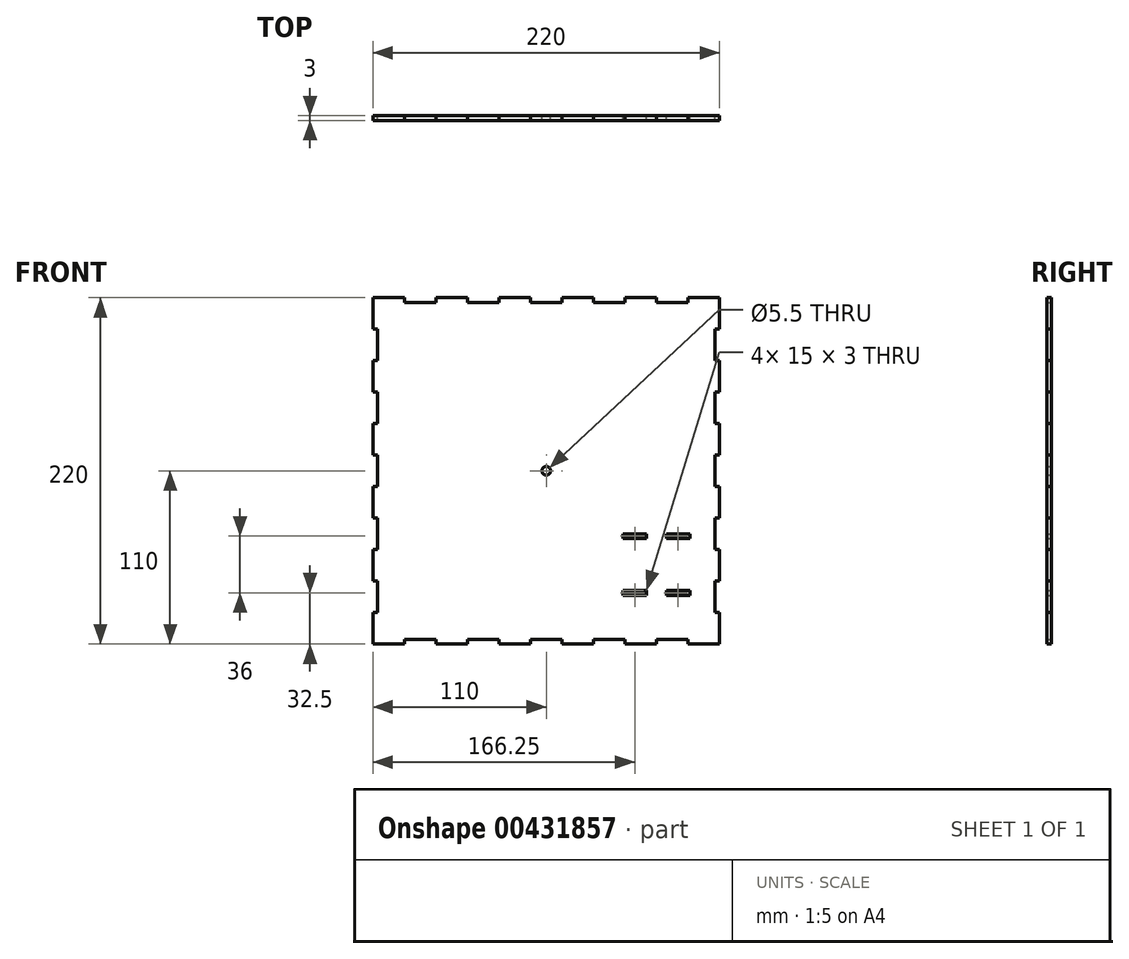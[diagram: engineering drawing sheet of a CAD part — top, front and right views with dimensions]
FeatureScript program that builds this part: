
annotation { "Feature Type Name" : "Feature", "Feature Type Description" : "" }
export const myFeature = defineFeature(function(context is Context, id is Id, definition is map)
    precondition{}
    {
        {
            var Q0;
            Q0=qCreatedBy(makeId("Front.planeOp"),FACE);
            var sketch = newSketch(context, id + "F0", { "sketchPlane" : qUnion([Q0])});
            skLineSegment(sketch, "E0.bottom", {"start": v(-110, 110) * mm, "end": v(-90, 110) * mm});
            skLineSegment(sketch, "E0.top", {"start": v(-110, -110) * mm, "end": v(-90, -110) * mm});
            skLineSegment(sketch, "E0.left", {"start": v(-110, 110) * mm, "end": v(-110, 90) * mm});
            skLineSegment(sketch, "E0.right", {"start": v(110, 110) * mm, "end": v(110, 90) * mm});
            skPoint(sketch, "E0.middle", {"position": v(0, 0) * mm});
            skCircle(sketch, "E1", {"center": v(0, 0) * mm, "radius": 2.75 * mm});
            skLineSegment(sketch, "E2.bottom", {"start": v(63.75, -40) * mm, "end": v(48.75, -40) * mm});
            skLineSegment(sketch, "E2.top", {"start": v(63.75, -43) * mm, "end": v(48.75, -43) * mm});
            skLineSegment(sketch, "E2.left", {"start": v(63.75, -40) * mm, "end": v(63.75, -43) * mm});
            skLineSegment(sketch, "E2.right", {"start": v(48.75, -40) * mm, "end": v(48.75, -43) * mm});
            skLineSegment(sketch, "E3.bottom", {"start": v(76.25, -40) * mm, "end": v(91.25, -40) * mm});
            skLineSegment(sketch, "E3.top", {"start": v(76.25, -43) * mm, "end": v(91.25, -43) * mm});
            skLineSegment(sketch, "E3.left", {"start": v(76.25, -40) * mm, "end": v(76.25, -43) * mm});
            skLineSegment(sketch, "E3.right", {"start": v(91.25, -40) * mm, "end": v(91.25, -43) * mm});
            skLineSegment(sketch, "E4.bottom", {"start": v(48.75, -76) * mm, "end": v(63.75, -76) * mm});
            skLineSegment(sketch, "E4.top", {"start": v(48.75, -79) * mm, "end": v(63.75, -79) * mm});
            skLineSegment(sketch, "E4.left", {"start": v(48.75, -76) * mm, "end": v(48.75, -79) * mm});
            skLineSegment(sketch, "E4.right", {"start": v(63.75, -76) * mm, "end": v(63.75, -79) * mm});
            skLineSegment(sketch, "E5.bottom", {"start": v(91.25, -76) * mm, "end": v(76.25, -76) * mm});
            skLineSegment(sketch, "E5.top", {"start": v(91.25, -79) * mm, "end": v(76.25, -79) * mm});
            skLineSegment(sketch, "E5.left", {"start": v(91.25, -76) * mm, "end": v(91.25, -79) * mm});
            skLineSegment(sketch, "E5.right", {"start": v(76.25, -76) * mm, "end": v(76.25, -79) * mm});
            skLineSegment(sketch, "E6.bottom", {"start": v(-10, -107) * mm, "end": v(10, -107) * mm});
            skLineSegment(sketch, "E6.left", {"start": v(-10, -107) * mm, "end": v(-10, -110) * mm});
            skLineSegment(sketch, "E6.right", {"start": v(10, -107) * mm, "end": v(10, -110) * mm});
            skPoint(sketch, "E6.middle", {"position": v(0, -110) * mm});
            skLineSegment(sketch, "E7.bottom", {"start": v(-50, -107) * mm, "end": v(-30, -107) * mm});
            skLineSegment(sketch, "E7.left", {"start": v(-50, -107) * mm, "end": v(-50, -110) * mm});
            skLineSegment(sketch, "E7.right", {"start": v(-30, -107) * mm, "end": v(-30, -110) * mm});
            skPoint(sketch, "E7.middle", {"position": v(-40, -110) * mm});
            skLineSegment(sketch, "E8.bottom", {"start": v(-90, -107) * mm, "end": v(-70, -107) * mm});
            skLineSegment(sketch, "E8.left", {"start": v(-90, -107) * mm, "end": v(-90, -110) * mm});
            skLineSegment(sketch, "E8.right", {"start": v(-70, -107) * mm, "end": v(-70, -110) * mm});
            skPoint(sketch, "E8.middle", {"position": v(-80, -110) * mm});
            skLineSegment(sketch, "E9.bottom", {"start": v(50, -107) * mm, "end": v(30, -107) * mm});
            skLineSegment(sketch, "E9.left", {"start": v(50, -107) * mm, "end": v(50, -110) * mm});
            skLineSegment(sketch, "E9.right", {"start": v(30, -107) * mm, "end": v(30, -110) * mm});
            skPoint(sketch, "E9.middle", {"position": v(40, -110) * mm});
            skLineSegment(sketch, "E10.bottom", {"start": v(70, -107) * mm, "end": v(90, -107) * mm});
            skLineSegment(sketch, "E10.left", {"start": v(70, -107) * mm, "end": v(70, -110) * mm});
            skLineSegment(sketch, "E10.right", {"start": v(90, -107) * mm, "end": v(90, -110) * mm});
            skPoint(sketch, "E10.middle", {"position": v(80, -110) * mm});
            skPoint(sketch, "E11.middle", {"position": v(92.14, -110) * mm});
            skLineSegment(sketch, "E12.trimOffspring", {"start": v(-70, -110) * mm, "end": v(-50, -110) * mm});
            skPoint(sketch, "E13.orphan", {"position": v(-90, -113) * mm});
            skPoint(sketch, "E14.orphan", {"position": v(-70, -113) * mm});
            skLineSegment(sketch, "E15.trimOffspring", {"start": v(-30, -110) * mm, "end": v(-10, -110) * mm});
            skPoint(sketch, "E16.orphan", {"position": v(-30, -113) * mm});
            skPoint(sketch, "E17.orphan", {"position": v(-50, -113) * mm});
            skLineSegment(sketch, "E18.trimOffspring", {"start": v(10, -110) * mm, "end": v(30, -110) * mm});
            skPoint(sketch, "E6.top.end.orphan", {"position": v(10, -113) * mm});
            skPoint(sketch, "E6.top.start.orphan", {"position": v(-10, -113) * mm});
            skLineSegment(sketch, "E19.trimOffspring", {"start": v(50, -110) * mm, "end": v(70, -110) * mm});
            skPoint(sketch, "E9.top.start.orphan", {"position": v(50, -113) * mm});
            skPoint(sketch, "E20.orphan", {"position": v(30, -113) * mm});
            skLineSegment(sketch, "E21.trimOffspring", {"start": v(90, -110) * mm, "end": v(110, -110) * mm});
            skPoint(sketch, "E22.orphan", {"position": v(90, -113) * mm});
            skPoint(sketch, "E23.orphan", {"position": v(70, -113) * mm});
            skLineSegment(sketch, "E24.bottom", {"start": v(-110, 10) * mm, "end": v(-107, 10) * mm});
            skLineSegment(sketch, "E24.top", {"start": v(-110, -10) * mm, "end": v(-107, -10) * mm});
            skLineSegment(sketch, "E24.right", {"start": v(-107, 10) * mm, "end": v(-107, -10) * mm});
            skPoint(sketch, "E24.middle", {"position": v(-110, 0) * mm});
            skLineSegment(sketch, "E25.bottom", {"start": v(-110, 50) * mm, "end": v(-107, 50) * mm});
            skLineSegment(sketch, "E25.top", {"start": v(-110, 30) * mm, "end": v(-107, 30) * mm});
            skLineSegment(sketch, "E25.right", {"start": v(-107, 50) * mm, "end": v(-107, 30) * mm});
            skPoint(sketch, "E25.middle", {"position": v(-110, 40) * mm});
            skLineSegment(sketch, "E26.bottom", {"start": v(-110, -30) * mm, "end": v(-107, -30) * mm});
            skLineSegment(sketch, "E26.top", {"start": v(-110, -50) * mm, "end": v(-107, -50) * mm});
            skLineSegment(sketch, "E26.right", {"start": v(-107, -30) * mm, "end": v(-107, -50) * mm});
            skPoint(sketch, "E26.middle", {"position": v(-110, -40) * mm});
            skLineSegment(sketch, "E27.bottom", {"start": v(-110, -70) * mm, "end": v(-107, -70) * mm});
            skLineSegment(sketch, "E27.top", {"start": v(-110, -90) * mm, "end": v(-107, -90) * mm});
            skLineSegment(sketch, "E27.right", {"start": v(-107, -70) * mm, "end": v(-107, -90) * mm});
            skPoint(sketch, "E27.middle", {"position": v(-110, -80) * mm});
            skLineSegment(sketch, "E28.bottom", {"start": v(-110, 90) * mm, "end": v(-107, 90) * mm});
            skLineSegment(sketch, "E28.top", {"start": v(-110, 70) * mm, "end": v(-107, 70) * mm});
            skLineSegment(sketch, "E28.right", {"start": v(-107, 90) * mm, "end": v(-107, 70) * mm});
            skPoint(sketch, "E28.middle", {"position": v(-110, 80) * mm});
            skPoint(sketch, "E29.orphan", {"position": v(-113, 90) * mm});
            skLineSegment(sketch, "E30.trimOffspring", {"start": v(-110, 70) * mm, "end": v(-110, 50) * mm});
            skPoint(sketch, "E31.orphan", {"position": v(-113, 70) * mm});
            skLineSegment(sketch, "E32.trimOffspring", {"start": v(-110, 30) * mm, "end": v(-110, 10) * mm});
            skPoint(sketch, "E33.orphan", {"position": v(-113, 50) * mm});
            skPoint(sketch, "E34.orphan", {"position": v(-113, 30) * mm});
            skPoint(sketch, "E24.left.start.orphan", {"position": v(-113, 10) * mm});
            skLineSegment(sketch, "E35.trimOffspring", {"start": v(-110, -10) * mm, "end": v(-110, -30) * mm});
            skPoint(sketch, "E36.orphan", {"position": v(-113, -10) * mm});
            skPoint(sketch, "E26.left.start.orphan", {"position": v(-113, -30) * mm});
            skLineSegment(sketch, "E37.trimOffspring", {"start": v(-110, -50) * mm, "end": v(-110, -70) * mm});
            skPoint(sketch, "E38.orphan", {"position": v(-113, -50) * mm});
            skPoint(sketch, "E27.left.start.orphan", {"position": v(-113, -70) * mm});
            skLineSegment(sketch, "E39.trimOffspring", {"start": v(-110, -90) * mm, "end": v(-110, -110) * mm});
            skPoint(sketch, "E40.orphan", {"position": v(-113, -90) * mm});
            skLineSegment(sketch, "E41.top", {"start": v(-10, 107) * mm, "end": v(10, 107) * mm});
            skLineSegment(sketch, "E41.left", {"start": v(-10, 110) * mm, "end": v(-10, 107) * mm});
            skLineSegment(sketch, "E41.right", {"start": v(10, 110) * mm, "end": v(10, 107) * mm});
            skPoint(sketch, "E41.middle", {"position": v(0, 110) * mm});
            skLineSegment(sketch, "E42.top", {"start": v(30, 107) * mm, "end": v(50, 107) * mm});
            skLineSegment(sketch, "E42.left", {"start": v(30, 110) * mm, "end": v(30, 107) * mm});
            skLineSegment(sketch, "E42.right", {"start": v(50, 110) * mm, "end": v(50, 107) * mm});
            skPoint(sketch, "E42.middle", {"position": v(40, 110) * mm});
            skLineSegment(sketch, "E43.top", {"start": v(70, 107) * mm, "end": v(90, 107) * mm});
            skLineSegment(sketch, "E43.left", {"start": v(70, 110) * mm, "end": v(70, 107) * mm});
            skLineSegment(sketch, "E43.right", {"start": v(90, 110) * mm, "end": v(90, 107) * mm});
            skPoint(sketch, "E43.middle", {"position": v(80, 110) * mm});
            skLineSegment(sketch, "E44.top", {"start": v(-50, 107) * mm, "end": v(-30, 107) * mm});
            skLineSegment(sketch, "E44.left", {"start": v(-50, 110) * mm, "end": v(-50, 107) * mm});
            skLineSegment(sketch, "E44.right", {"start": v(-30, 110) * mm, "end": v(-30, 107) * mm});
            skPoint(sketch, "E44.middle", {"position": v(-40, 110) * mm});
            skLineSegment(sketch, "E45.top", {"start": v(-90, 107) * mm, "end": v(-70, 107) * mm});
            skLineSegment(sketch, "E45.left", {"start": v(-90, 110) * mm, "end": v(-90, 107) * mm});
            skLineSegment(sketch, "E45.right", {"start": v(-70, 110) * mm, "end": v(-70, 107) * mm});
            skPoint(sketch, "E45.middle", {"position": v(-80, 110) * mm});
            skPoint(sketch, "E46.orphan", {"position": v(-70, 113) * mm});
            skLineSegment(sketch, "E47.trimOffspring", {"start": v(-70, 110) * mm, "end": v(-50, 110) * mm});
            skPoint(sketch, "E48.orphan", {"position": v(-90, 113) * mm});
            skPoint(sketch, "E49.orphan", {"position": v(-50, 113) * mm});
            skLineSegment(sketch, "E50.trimOffspring", {"start": v(-30, 110) * mm, "end": v(-10, 110) * mm});
            skPoint(sketch, "E51.orphan", {"position": v(-30, 113) * mm});
            skPoint(sketch, "E52.orphan", {"position": v(-10, 113) * mm});
            skLineSegment(sketch, "E53.trimOffspring", {"start": v(10, 110) * mm, "end": v(30, 110) * mm});
            skPoint(sketch, "E54.orphan", {"position": v(10, 113) * mm});
            skPoint(sketch, "E42.bottom.start.orphan", {"position": v(30, 113) * mm});
            skLineSegment(sketch, "E55.trimOffspring", {"start": v(50, 110) * mm, "end": v(70, 110) * mm});
            skPoint(sketch, "E56.orphan", {"position": v(50, 113) * mm});
            skPoint(sketch, "E57.orphan", {"position": v(70, 113) * mm});
            skLineSegment(sketch, "E58.trimOffspring", {"start": v(90, 110) * mm, "end": v(110, 110) * mm});
            skPoint(sketch, "E59.orphan", {"position": v(90, 113) * mm});
            skLineSegment(sketch, "E60.bottom", {"start": v(107, 10) * mm, "end": v(110, 10) * mm});
            skLineSegment(sketch, "E60.top", {"start": v(107, -10) * mm, "end": v(110, -10) * mm});
            skLineSegment(sketch, "E60.left", {"start": v(107, 10) * mm, "end": v(107, -10) * mm});
            skPoint(sketch, "E60.middle", {"position": v(110, 0) * mm});
            skLineSegment(sketch, "E61.bottom", {"start": v(107, -50) * mm, "end": v(110, -50) * mm});
            skLineSegment(sketch, "E61.top", {"start": v(107, -30) * mm, "end": v(110, -30) * mm});
            skLineSegment(sketch, "E61.left", {"start": v(107, -50) * mm, "end": v(107, -30) * mm});
            skPoint(sketch, "E61.middle", {"position": v(110, -40) * mm});
            skLineSegment(sketch, "E62.bottom", {"start": v(107, -70) * mm, "end": v(110, -70) * mm});
            skLineSegment(sketch, "E62.top", {"start": v(107, -90) * mm, "end": v(110, -90) * mm});
            skLineSegment(sketch, "E62.left", {"start": v(107, -70) * mm, "end": v(107, -90) * mm});
            skPoint(sketch, "E62.middle", {"position": v(110, -80) * mm});
            skLineSegment(sketch, "E63.bottom", {"start": v(107, 50) * mm, "end": v(110, 50) * mm});
            skLineSegment(sketch, "E63.top", {"start": v(107, 30) * mm, "end": v(110, 30) * mm});
            skLineSegment(sketch, "E63.left", {"start": v(107, 50) * mm, "end": v(107, 30) * mm});
            skPoint(sketch, "E63.middle", {"position": v(110, 40) * mm});
            skLineSegment(sketch, "E64.bottom", {"start": v(107, 70) * mm, "end": v(110, 70) * mm});
            skLineSegment(sketch, "E64.top", {"start": v(107, 90) * mm, "end": v(110, 90) * mm});
            skLineSegment(sketch, "E64.left", {"start": v(107, 70) * mm, "end": v(107, 90) * mm});
            skPoint(sketch, "E64.middle", {"position": v(110, 80) * mm});
            skPoint(sketch, "E65.orphan", {"position": v(113, 10) * mm});
            skLineSegment(sketch, "E66.trimOffspring", {"start": v(110, -10) * mm, "end": v(110, -30) * mm});
            skPoint(sketch, "E67.orphan", {"position": v(113, -10) * mm});
            skPoint(sketch, "E68.orphan", {"position": v(113, -50) * mm});
            skLineSegment(sketch, "E69.trimOffspring", {"start": v(110, -50) * mm, "end": v(110, -70) * mm});
            skPoint(sketch, "E70.orphan", {"position": v(113, -30) * mm});
            skPoint(sketch, "E71.orphan", {"position": v(113, 30) * mm});
            skLineSegment(sketch, "E72.trimOffspring", {"start": v(110, 30) * mm, "end": v(110, 10) * mm});
            skPoint(sketch, "E73.orphan", {"position": v(113, 50) * mm});
            skPoint(sketch, "E64.right.end.orphan", {"position": v(113, 90) * mm});
            skPoint(sketch, "E74.orphan", {"position": v(113, 70) * mm});
            skLineSegment(sketch, "E75.trimOffspring", {"start": v(110, 70) * mm, "end": v(110, 50) * mm});
            skPoint(sketch, "E76.orphan", {"position": v(113, -70) * mm});
            skLineSegment(sketch, "E77.trimOffspring", {"start": v(110, -90) * mm, "end": v(110, -110) * mm});
            skPoint(sketch, "E78.orphan", {"position": v(113, -90) * mm});
            skSolve(sketch);
        }
        {
            var Q0;
            Q0=makeQuery(id+"F0.imprint","IMPRINT",FACE,{"disambiguationData":[TD([[makeQuery(id+"F0.imprint","IMPRINT",EDGE,{"derivedFrom":sQuery(id+"F0.wireOp",EDGE,"E0.bottom")}),-1.0]])]});
            extrude(context, id + "F1", {"entities" : qUnion([Q0]), "depth" : 3 * mm});
        }
    });
